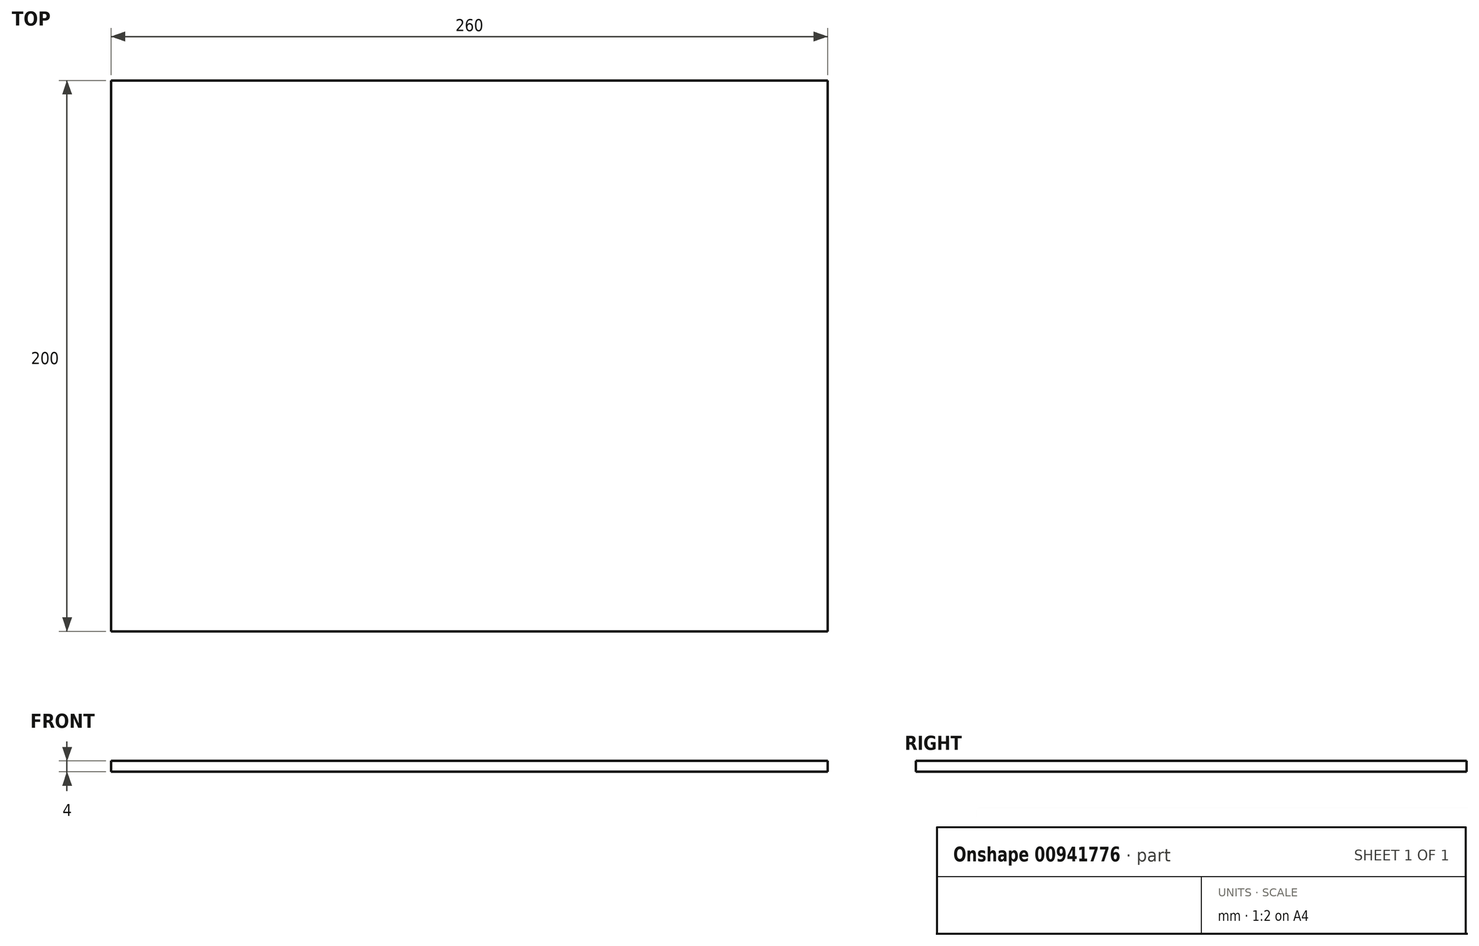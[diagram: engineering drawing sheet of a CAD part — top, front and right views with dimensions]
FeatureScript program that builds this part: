
annotation { "Feature Type Name" : "Feature", "Feature Type Description" : "" }
export const myFeature = defineFeature(function(context is Context, id is Id, definition is map)
    precondition{}
    {
        {
            var Q0;
            Q0=qCreatedBy(makeId("Top.planeOp"),FACE);
            var sketch = newSketch(context, id + "F0", { "sketchPlane" : qUnion([Q0])});
            skLineSegment(sketch, "E0.bottom", {"start": v(-130, 100) * mm, "end": v(130, 100) * mm});
            skLineSegment(sketch, "E0.top", {"start": v(-130, -100) * mm, "end": v(130, -100) * mm});
            skLineSegment(sketch, "E0.left", {"start": v(-130, 100) * mm, "end": v(-130, -100) * mm});
            skLineSegment(sketch, "E0.right", {"start": v(130, 100) * mm, "end": v(130, -100) * mm});
            skSolve(sketch);
        }
        {
            var Q0;
            Q0=qSketchRegion(id+"F0",true);
            extrude(context, id + "F1", {"entities" : qUnion([Q0]), "oppositeDirection" : true, "depth" : 4 * mm, "offsetDistance" : 25 * mm});
        }
    });
